# Revit family: Electronics_Community-Point-Source_Biamp_Loudspeaker_R_25
name_source: partatom
category: Communication Devices
units: mm (PartAtom-declared; Revit-internal decimal feet)

## family parameters
Cut with Voids When Loaded = No
Host = Face
Maintain Annotation Orientation = No
OmniClass Number = 23.85.10.11.14.14.14
Part Type = Normal
Room Calculation Point = No
Round Connector Dimension = Use Diameter
Shared = No

## types (2) — shared parameters
Default Elevation = 4' - 0"
Depth = 1' - 1 1/2"
Description = R.25 Two-Way Coaxial Horn-Loaded 90° x 40° Weather-Resistant Loudspeaker
Environmental = IP55W per IEC 529, designed to MIL-STD-810G
Equalized Maximum SPL = Peak - 125dB; Continuous -119dB
Equalized Sensitivity = 1W/1m - 96dB; 2.83V - 96dB
Finish = Refer to the Technical Drawing (page 3)
Grill Material = Biamp - Plastic - Gray(Grid)
Height = 0' - 11 1/2"
Housing Material = Biamp - Plastic - Gray
Included Accessories = Zinc-rich epoxy dual-layer powder-coated yoke
Input Connection = 16-2 SJOW cable (12 ft / 4m), with stripped ends
Manufacturer = Biamp
Max value position = 3
Mounting Points = Five (5) M8 rigging points, 1-3/8 pole mount socket
Nominal Beamwidth  (H x V) = 90° x 40°
Nominal Maximum SPL (Whole Space) = Peak - 128dB; Continuous -120dB
Nominal Sensitivity = 1W/1m - 97dB; 2.83V - 97dB
Operating Environment = Indoor or Weather-Resistant Outdoor
Operating Mode = Passive - Low Impedance or 70V/100V models
Operating Range = 100 Hz to 16 kHz
Product Documentation Link = https://downloads.biamp.com
Product Page URL = https://www.biamp.com
Product data url = https://www.bimobject.com
Required Accessories = High Pass Filter - 100 Hz, 24 dB /octave, Digital Signal Processor
Transducers = LF   1 x 8 (203mm) carbon ring, hydrophobic cone, 2.5 (64mm) HF 1 x 3/4 (19mm)  exit, non-metallic Ferrofuid-cooled comp driver DYNA-TECH protection circuitry for drivers
URL = https://www.biamp.com
Width = 0' - 11 1/2"
Yoke Material = Biamp - Metal - Gray

## per-type parameters (varying)
| type | Connector Description | Controls | Recommended Amplifers | Weight |
| R.25-94Z | Terminal strip, Low Impedance | None |  | 20.06 lb |
| R.25-94TZ | Terminal strip, 70V/100V operation | 4-position tap selection rotary switch (behind plug) | 200W - 400W @ 8 Ohms,  (40V - 57V) | 22.93 lb |

note: column(s) folded — value = type name in every type: Model

## geometry (parser evidence)
native form markers: Sweep x2
no freeform markers — native parametric forms only
